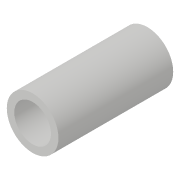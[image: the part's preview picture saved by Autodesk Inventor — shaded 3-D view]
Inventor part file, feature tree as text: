
AUTODESK INVENTOR PART (.ipt)
format: ipt  version: 2018 (Build 220112000, 112)  size: 86,528 bytes
history: native  units: in
note: dims shown in document units (in); Inventor stores cm internally (conversion verified against a paired STEP export)
features: extrude x1
ambient origin geometry x8: Origin, YZ Plane, XZ Plane, XY Plane, X Axis, Y Axis, Z Axis, Center Point
bodies: Solid1 (feature_tree)
feature tree (1):
  extrude  "Extrude1"  [1 undecoded]
note: 1 required parameter value undecoded (feature->parameter linkage not recoverable at this tier; creation-order binding heuristic only, values carry confidence <= 0.55)
